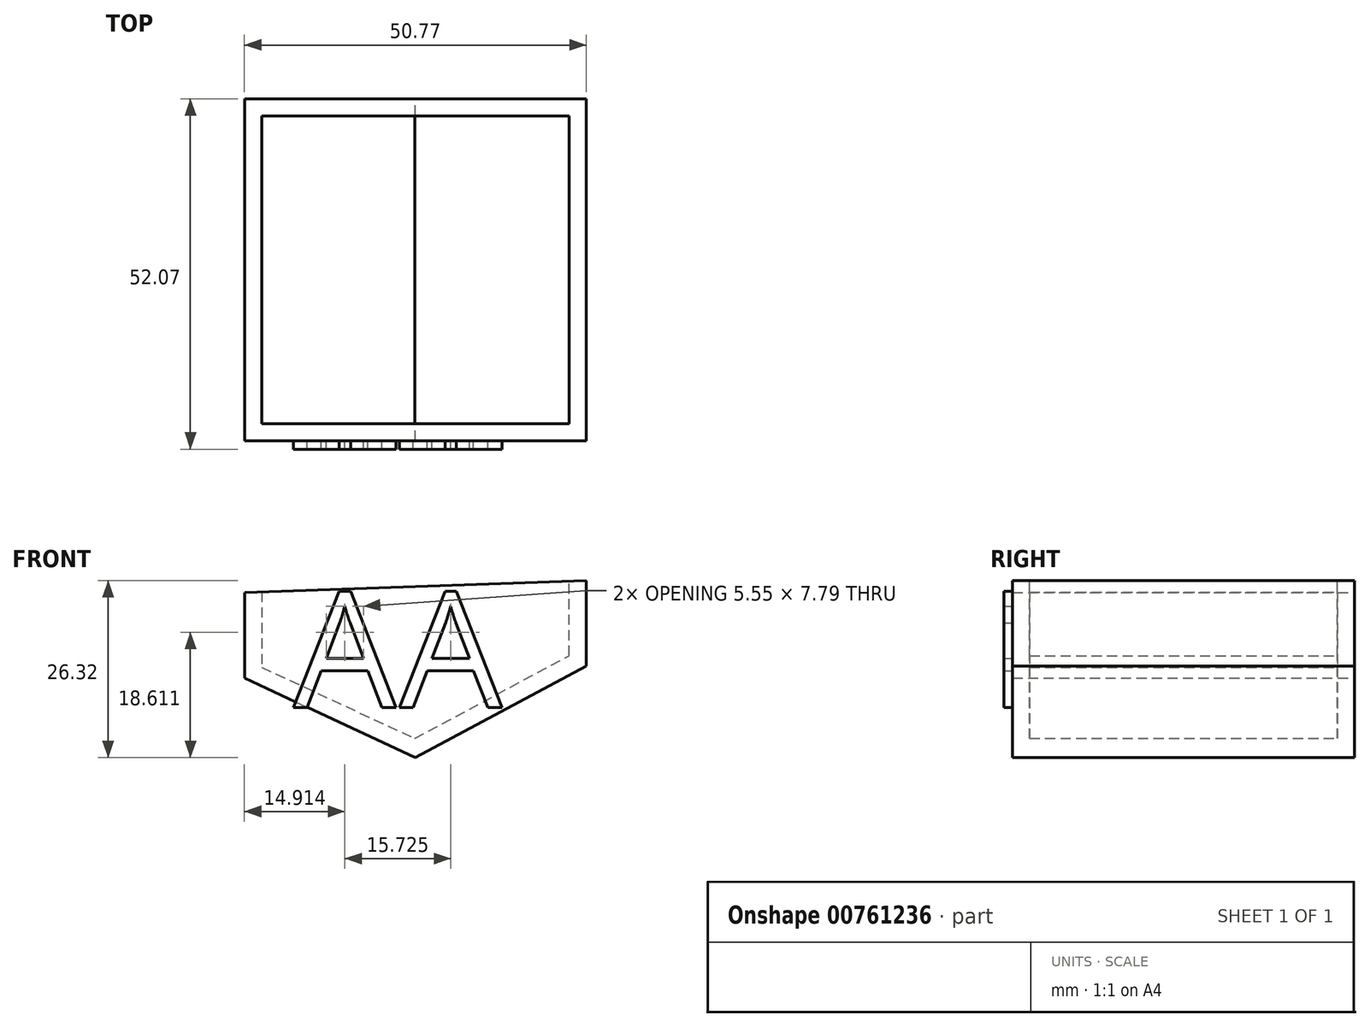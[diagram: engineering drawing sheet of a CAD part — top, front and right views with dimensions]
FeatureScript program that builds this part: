
annotation { "Feature Type Name" : "Feature", "Feature Type Description" : "" }
export const myFeature = defineFeature(function(context is Context, id is Id, definition is map)
    precondition{}
    {
        {
            var Q0;
            Q0=qCreatedBy(makeId("Front.planeOp"),FACE);
            var sketch = newSketch(context, id + "F0", { "sketchPlane" : qUnion([Q0])});
            skLineSegment(sketch, "E0", {"start": v(-53.38, 39.72) * mm, "end": v(-53.38, 27.02) * mm});
            skLineSegment(sketch, "E1", {"start": v(-2.6, 28.82) * mm, "end": v(-2.6, 41.52) * mm});
            skLineSegment(sketch, "E2", {"start": v(-53.38, 39.72) * mm, "end": v(-2.6, 41.52) * mm});
            skLineSegment(sketch, "E3", {"start": v(-53.38, 27.02) * mm, "end": v(-28, 15.2) * mm});
            skLineSegment(sketch, "E4", {"start": v(-28, 15.2) * mm, "end": v(-2.6, 28.82) * mm});
            skPoint(sketch, "E5.orphan", {"position": v(-2.6, 16.12) * mm});
            skPoint(sketch, "E6.orphan", {"position": v(-53.38, 14.32) * mm});
            skSolve(sketch);
        }
        {
            var Q0;
            Q0=makeQuery(id+"F0.imprint","IMPRINT",FACE,{"disambiguationData":[TD([[makeQuery(id+"F0.imprint","IMPRINT",EDGE,{"derivedFrom":sQuery(id+"F0.wireOp",EDGE,"E0")}),1.0]])]});
            extrude(context, id + "F1", {"entities" : qUnion([Q0]), "depth" : 50.8 * mm, "offsetDistance" : 25.4 * mm});
        }
        {
            var Q0;
            Q0=makeQuery(id+"F1.opExtrude","SWEPT_FACE",FACE,{"disambiguationData":[OSD([sQuery(id+"F0.wireOp",EDGE,"E2")])]});
            shell(context, id + "F2", {"entities" : qUnion([Q0]), "thickness" : 2.54 * mm});
        }
        {
            var Q0;
            Q0=makeQuery(id+"F1.opExtrude","CAP_FACE",FACE,{"disambiguationData":[OSD([sQuery(id+"F0.wireOp",EDGE,"E0"),sQuery(id+"F0.wireOp",EDGE,"E1"),sQuery(id+"F0.wireOp",EDGE,"E2"),sQuery(id+"F0.wireOp",EDGE,"E3"),sQuery(id+"F0.wireOp",EDGE,"E4")])],"isStart":false});
            var sketch = newSketch(context, id + "F3", { "sketchPlane" : qUnion([Q0])});
            skText(sketch, "E7", { "text": "AA", "fontName": "OpenSans-Regular.ttf"});
            const initialGuessF3  = {"E7": [-0.04608, 0.02266, 1, 0, 0.01731]};
            skSetInitialGuess(sketch, initialGuessF3);
            skSolve(sketch);
        }
        {
            var Q0;
            Q0 = qSketchRegion(id + "F3", true);
            extrude(context, id + "F4", {"entities" : qUnion([Q0]), "depth" : 1.27 * mm, "offsetDistance" : 25.4 * mm});
        }
    });
